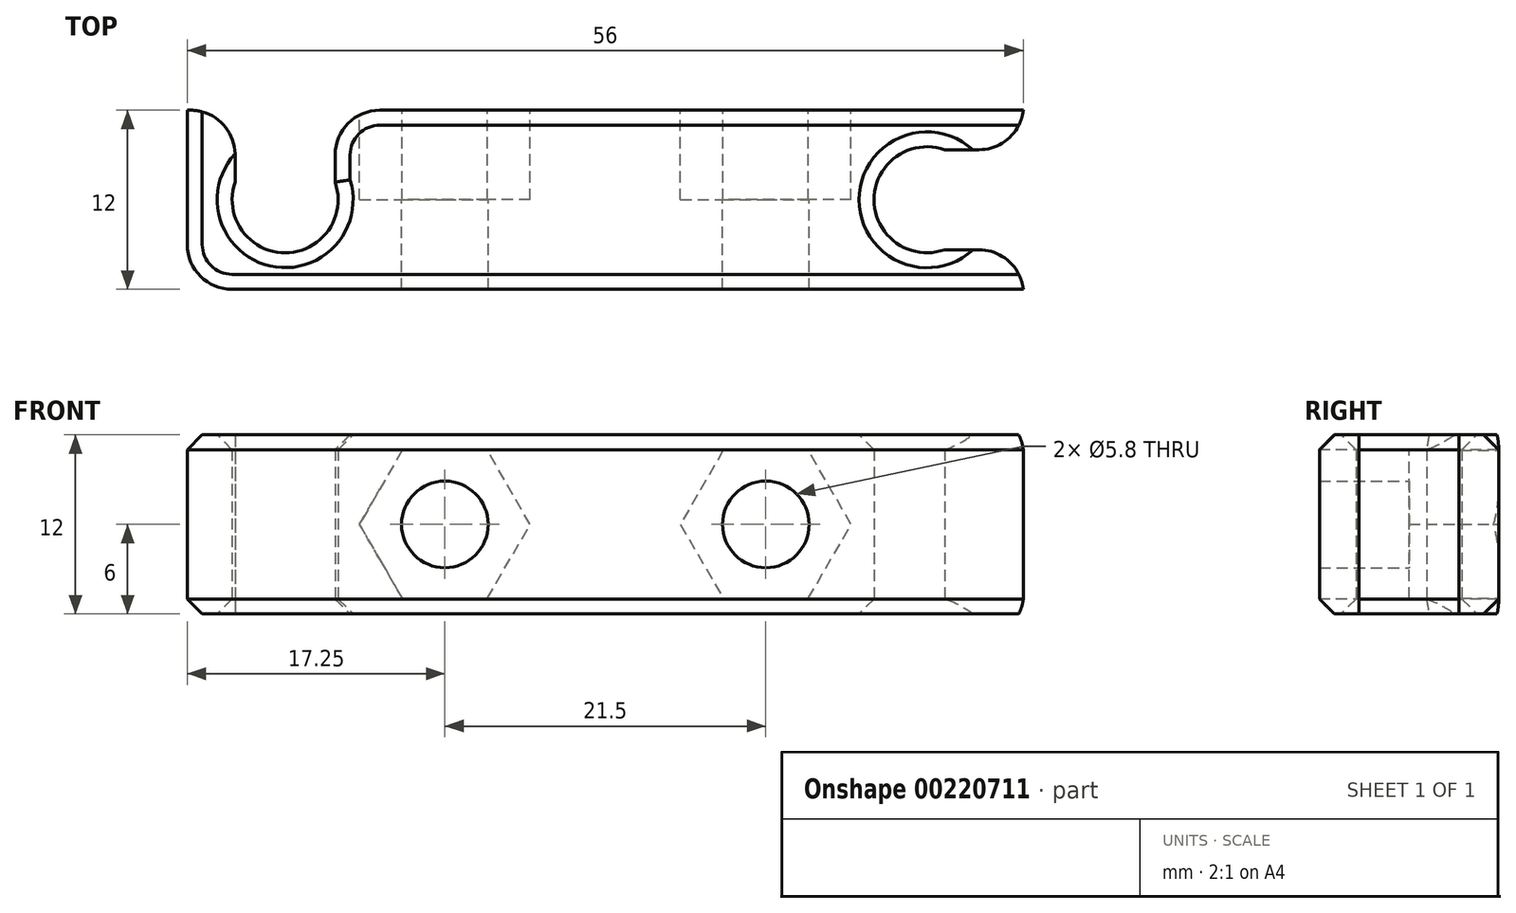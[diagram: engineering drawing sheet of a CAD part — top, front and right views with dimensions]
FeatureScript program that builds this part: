
annotation { "Feature Type Name" : "Feature", "Feature Type Description" : "" }
export const myFeature = defineFeature(function(context is Context, id is Id, definition is map)
    precondition{}
    {
        {
            var Q0;
            Q0=qCreatedBy(makeId("Top.planeOp"),FACE);
            var sketch = newSketch(context, id + "F0", { "sketchPlane" : qUnion([Q0])});
            skLineSegment(sketch, "E0.bottom", {"start": v(-28, 6) * mm, "end": v(28, 6) * mm});
            skLineSegment(sketch, "E0.top", {"start": v(-28, -6) * mm, "end": v(28, -6) * mm});
            skLineSegment(sketch, "E0.left", {"start": v(-28, 6) * mm, "end": v(-28, -6) * mm});
            skLineSegment(sketch, "E0.right", {"start": v(28, 6) * mm, "end": v(28, -6) * mm});
            skPoint(sketch, "E0.middle", {"position": v(0, 0) * mm});
            skCircle(sketch, "E1", {"center": v(-21.45, 0) * mm, "radius": 3.55 * mm});
            skCircle(sketch, "E2.1.0.0", {"center": v(21.55, 0) * mm, "radius": 3.55 * mm});
            skLineSegment(sketch, "E2.direction1", {"start": v(-21.45, 0) * mm, "end": v(21.55, 0) * mm, "construction": true});
            skLineSegment(sketch, "E3", {"start": v(22.72, 3.35) * mm, "end": v(28, 3.35) * mm});
            skLineSegment(sketch, "E4", {"start": v(22.72, -3.35) * mm, "end": v(28, -3.35) * mm});
            skLineSegment(sketch, "E5", {"start": v(-24.8, 1.17) * mm, "end": v(-24.8, 6) * mm});
            skLineSegment(sketch, "E6", {"start": v(-18.1, 1.17) * mm, "end": v(-18.1, 6) * mm});
            skSolve(sketch);
        }
        {
            var Q0;
            {var subQ2=sQuery(id+"F0.wireOp",EDGE,"E0.top");Q0=makeQuery(id+"F0.imprint","IMPRINT",FACE,{"disambiguationData":[TD([[makeQuery(id+"F0.imprint","IMPRINT",EDGE,{"derivedFrom":subQ2}),1.0]])]});}
            extrude(context, id + "F1", {"entities" : qUnion([Q0]), "depth" : 12 * mm});
        }
        {
            var Q0;
            {var subQ0=sQuery(id+"F0.wireOp",EDGE,"E0.bottom");Q0=makeQuery(id+"F1.opExtrude","SWEPT_FACE",FACE,{"disambiguationData":[OSD([subQ0]),TDD([makeQuery(id+"F0.imprint","IMPRINT",EDGE,{"disambiguationData":[TD([[makeQuery(id+"F0.imprint","INTERSECT",VERTEX,{"derivedFrom":[subQ0,sQuery(id+"F0.wireOp",EDGE,"E0.right")]}),1.0]])],"derivedFrom":subQ0})])]});}
            var sketch = newSketch(context, id + "F2", { "sketchPlane" : qUnion([Q0])});
            skCircle(sketch, "E7", {"center": v(-10.75, 6) * mm, "radius": 2.9 * mm});
            skCircle(sketch, "E8.cCircle", {"center": v(-10.75, 6) * mm, "radius": 4.95 * mm, "construction": true});
            skLineSegment(sketch, "E8.0", {"start": v(-13.6, 10.95) * mm, "end": v(-7.9, 10.95) * mm});
            skLineSegment(sketch, "E8.1", {"start": v(-7.9, 10.95) * mm, "end": v(-5.03, 6) * mm});
            skLineSegment(sketch, "E8.2", {"start": v(-5.03, 6) * mm, "end": v(-7.9, 1.05) * mm});
            skLineSegment(sketch, "E8.3", {"start": v(-7.9, 1.05) * mm, "end": v(-13.6, 1.05) * mm});
            skLineSegment(sketch, "E8.4", {"start": v(-13.6, 1.05) * mm, "end": v(-16.47, 6) * mm});
            skLineSegment(sketch, "E8.5", {"start": v(-16.47, 6) * mm, "end": v(-13.6, 10.95) * mm});
            skPoint(sketch, "E8.0.midPoint", {"position": v(-10.75, 10.95) * mm});
            skCircle(sketch, "E9.1.0.0", {"center": v(10.75, 6) * mm, "radius": 2.9 * mm});
            skPoint(sketch, "E9.1.0.1", {"position": v(10.75, 10.95) * mm});
            skCircle(sketch, "E9.1.0.2", {"center": v(10.75, 6) * mm, "radius": 4.95 * mm, "construction": true});
            skLineSegment(sketch, "E9.1.0.3", {"start": v(7.9, 10.95) * mm, "end": v(13.6, 10.95) * mm});
            skLineSegment(sketch, "E9.1.0.4", {"start": v(13.6, 10.95) * mm, "end": v(16.47, 6) * mm});
            skLineSegment(sketch, "E9.1.0.5", {"start": v(16.47, 6) * mm, "end": v(13.6, 1.05) * mm});
            skLineSegment(sketch, "E9.1.0.6", {"start": v(13.6, 1.05) * mm, "end": v(7.9, 1.05) * mm});
            skLineSegment(sketch, "E9.1.0.7", {"start": v(7.9, 1.05) * mm, "end": v(5.03, 6) * mm});
            skLineSegment(sketch, "E9.1.0.8", {"start": v(5.03, 6) * mm, "end": v(7.9, 10.95) * mm});
            skLineSegment(sketch, "E9.direction1", {"start": v(-13.6, 1.05) * mm, "end": v(7.9, 1.05) * mm, "construction": true});
            skSolve(sketch);
        }
        {
            var Q0;
            Q0=makeQuery(id+"F1.opExtrude","SWEPT_EDGE",EDGE,{"disambiguationData":[OSD([sQuery(id+"F0.wireOp",EDGE,"E0.bottom"),sQuery(id+"F0.wireOp",EDGE,"E6")])]});
            var Q1;
            Q1=makeQuery(id+"F1.opExtrude","SWEPT_EDGE",EDGE,{"disambiguationData":[OSD([sQuery(id+"F0.wireOp",EDGE,"E0.bottom"),sQuery(id+"F0.wireOp",EDGE,"E5")])]});
            var Q2;
            Q2=makeQuery(id+"F1.opExtrude","SWEPT_EDGE",EDGE,{"disambiguationData":[OSD([sQuery(id+"F0.wireOp",EDGE,"E0.right"),sQuery(id+"F0.wireOp",EDGE,"E4")])]});
            var Q3;
            Q3=makeQuery(id+"F1.opExtrude","SWEPT_EDGE",EDGE,{"disambiguationData":[OSD([sQuery(id+"F0.wireOp",EDGE,"E0.top"),sQuery(id+"F0.wireOp",EDGE,"E0.left")])]});
            var Q4;
            Q4=makeQuery(id+"F1.opExtrude","SWEPT_EDGE",EDGE,{"disambiguationData":[OSD([sQuery(id+"F0.wireOp",EDGE,"E0.right"),sQuery(id+"F0.wireOp",EDGE,"E3")])]});
            fillet(context, id + "F3", {"entities" : qUnion([Q0, Q1, Q2, Q3, Q4]), "radius" : 3 * mm, "tangentPropagation" : true, "allowEdgeOverflow" : false});
        }
        {
            var Q0;
            Q0=makeQuery(id+"F1.opExtrude","CAP_EDGE",EDGE,{"disambiguationData":[OSD([sQuery(id+"F0.wireOp",EDGE,"E0.top")])],"isStart":false});
            var Q1;
            Q1=makeQuery(id+"F1.opExtrude","CAP_EDGE",EDGE,{"disambiguationData":[OSD([sQuery(id+"F0.wireOp",EDGE,"E0.top")])],"isStart":true});
            var Q2;
            Q2=makeQuery(id+"F1.opExtrude","CAP_EDGE",EDGE,{"disambiguationData":[OSD([sQuery(id+"F0.wireOp",EDGE,"E2.1.0.0")])],"isStart":false});
            var Q3;
            Q3=makeQuery(id+"F1.opExtrude","CAP_EDGE",EDGE,{"disambiguationData":[OSD([sQuery(id+"F0.wireOp",EDGE,"E1")])],"isStart":false});
            var Q4;
            Q4=makeQuery(id+"F1.opExtrude","CAP_EDGE",EDGE,{"disambiguationData":[OSD([sQuery(id+"F0.wireOp",EDGE,"E2.1.0.0")])],"isStart":true});
            var Q5;
            Q5=makeQuery(id+"F1.opExtrude","CAP_EDGE",EDGE,{"disambiguationData":[OSD([sQuery(id+"F0.wireOp",EDGE,"E1")])],"isStart":true});
            var Q6;
            {var subQ0=sQuery(id+"F0.wireOp",EDGE,"E0.bottom");Q6=makeQuery(id+"F1.opExtrude","CAP_EDGE",EDGE,{"disambiguationData":[OSD([subQ0]),TDD([makeQuery(id+"F0.imprint","IMPRINT",EDGE,{"disambiguationData":[TD([[makeQuery(id+"F0.imprint","INTERSECT",VERTEX,{"derivedFrom":[subQ0,sQuery(id+"F0.wireOp",EDGE,"E0.right")]}),1.0]])],"derivedFrom":subQ0})])],"isStart":true});}
            var Q7;
            {var subQ0=sQuery(id+"F0.wireOp",EDGE,"E0.bottom");Q7=makeQuery(id+"F1.opExtrude","CAP_EDGE",EDGE,{"disambiguationData":[OSD([subQ0]),TDD([makeQuery(id+"F0.imprint","IMPRINT",EDGE,{"disambiguationData":[TD([[makeQuery(id+"F0.imprint","INTERSECT",VERTEX,{"derivedFrom":[subQ0,sQuery(id+"F0.wireOp",EDGE,"E0.right")]}),1.0]])],"derivedFrom":subQ0})])],"isStart":false});}
            chamfer(context, id + "F4", {"entities" : qUnion([Q0, Q1, Q2, Q3, Q4, Q5, Q6, Q7]), "width" : 1 * mm, "tangentPropagation" : true});
        }
        {
            var Q0;
            Q0=makeQuery(id+"F2.imprint","IMPRINT",FACE,{"disambiguationData":[TD([[makeQuery(id+"F2.imprint","IMPRINT",EDGE,{"derivedFrom":sQuery(id+"F2.wireOp",EDGE,"E7")}),1.0]])]});
            var Q1;
            Q1=makeQuery(id+"F2.imprint","IMPRINT",FACE,{"disambiguationData":[TD([[makeQuery(id+"F2.imprint","IMPRINT",EDGE,{"derivedFrom":sQuery(id+"F2.wireOp",EDGE,"E9.1.0.0")}),1.0]])]});
            extrude(context, id + "F5", {"entities" : qUnion([Q0, Q1]), "operationType" : NewBodyOperationType.REMOVE, "endBound" : BoundingType.THROUGH_ALL, "oppositeDirection" : true, "depth" : 25 * mm});
        }
        {
            var Q0;
            Q0=makeQuery(id+"F2.imprint","IMPRINT",FACE,{"disambiguationData":[TD([[makeQuery(id+"F2.imprint","IMPRINT",EDGE,{"derivedFrom":sQuery(id+"F2.wireOp",EDGE,"E7")}),-1.0]])]});
            var Q1;
            Q1=makeQuery(id+"F2.imprint","IMPRINT",FACE,{"disambiguationData":[TD([[makeQuery(id+"F2.imprint","IMPRINT",EDGE,{"derivedFrom":sQuery(id+"F2.wireOp",EDGE,"E9.1.0.0")}),-1.0]])]});
            extrude(context, id + "F6", {"entities" : qUnion([Q0, Q1]), "operationType" : NewBodyOperationType.REMOVE, "oppositeDirection" : true, "depth" : 6 * mm});
        }
    });
